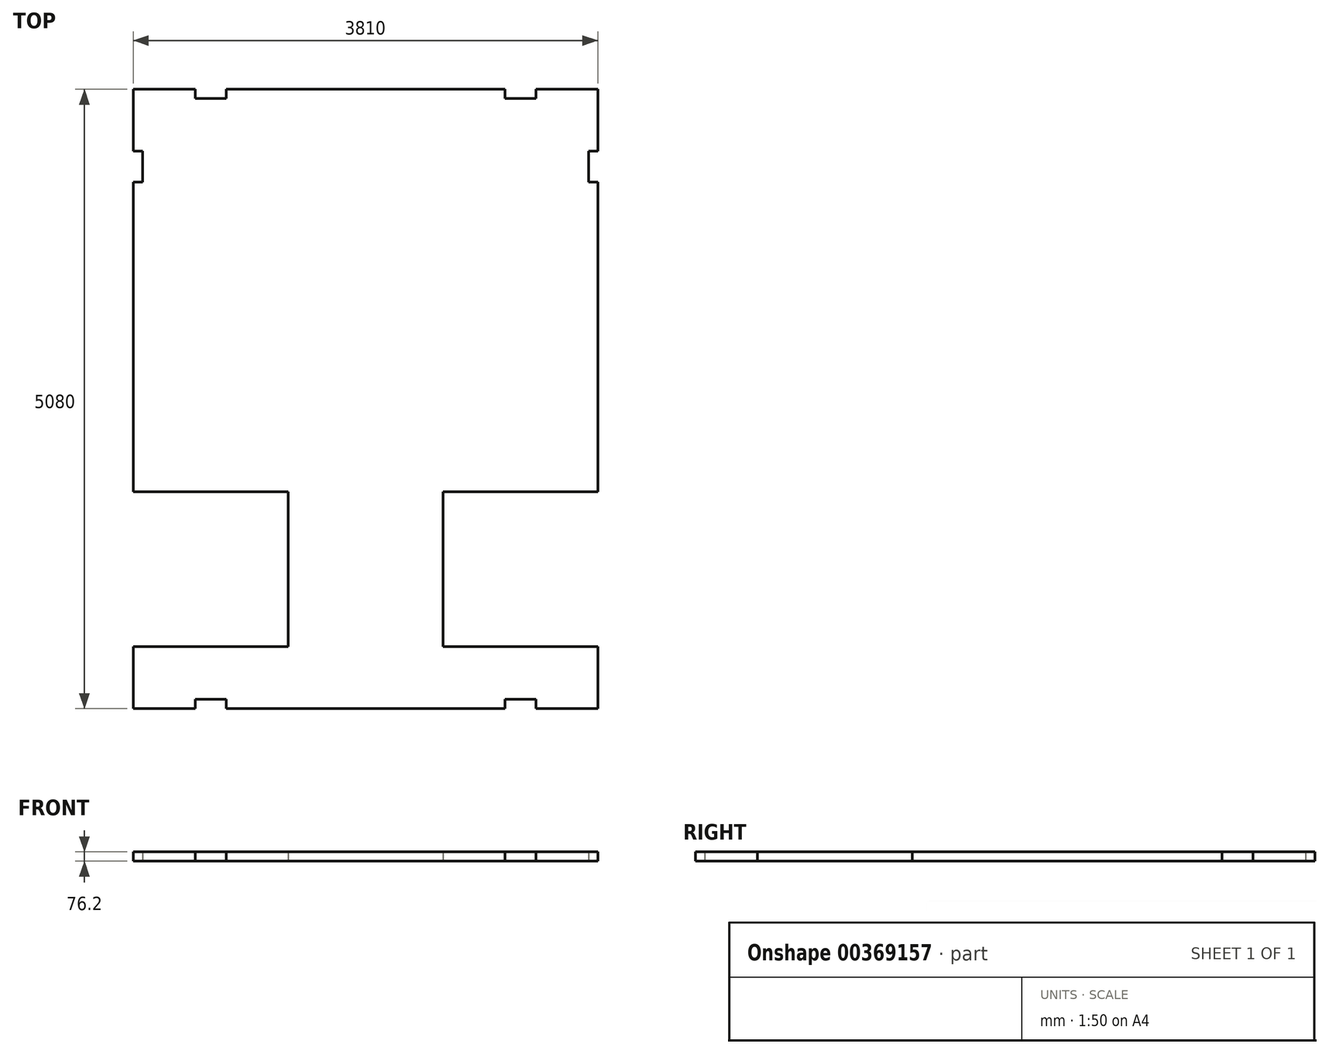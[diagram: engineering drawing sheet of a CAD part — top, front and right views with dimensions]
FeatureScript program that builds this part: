
annotation { "Feature Type Name" : "Feature", "Feature Type Description" : "" }
export const myFeature = defineFeature(function(context is Context, id is Id, definition is map)
    precondition{}
    {
        {
            var Q0;
            Q0=qCreatedBy(makeId("Top.planeOp"),FACE);
            var sketch = newSketch(context, id + "F0", { "sketchPlane" : qUnion([Q0])});
            skLineSegment(sketch, "E0.bottom", {"start": v(1905, 2540) * mm, "end": v(1397, 2540) * mm});
            skLineSegment(sketch, "E0.top", {"start": v(1143, -2540) * mm, "end": v(-1143, -2540) * mm});
            skLineSegment(sketch, "E0.left", {"start": v(1905, 2540) * mm, "end": v(1905, 2032) * mm});
            skLineSegment(sketch, "E0.right", {"start": v(-1905, 2540) * mm, "end": v(-1905, 2032) * mm});
            skPoint(sketch, "E0.middle", {"position": v(0, 0) * mm});
            skLineSegment(sketch, "E1", {"start": v(-1905, 1778) * mm, "end": v(-1828.8, 1778) * mm});
            skLineSegment(sketch, "E2", {"start": v(-1905, 2032) * mm, "end": v(-1828.8, 2032) * mm});
            skLineSegment(sketch, "E3", {"start": v(-1828.8, 2032) * mm, "end": v(-1828.8, 1778) * mm});
            skLineSegment(sketch, "E4.trimOffspring", {"start": v(-1905, 1778) * mm, "end": v(-1905, -762) * mm});
            skLineSegment(sketch, "E5", {"start": v(-1905, 2540) * mm, "end": v(-1397, 2540) * mm});
            skLineSegment(sketch, "E6", {"start": v(-1397, 2540) * mm, "end": v(-1143, 2540) * mm});
            skLineSegment(sketch, "E7", {"start": v(-1397, 2540) * mm, "end": v(-1397, 2463.8) * mm});
            skLineSegment(sketch, "E8", {"start": v(-1397, 2463.8) * mm, "end": v(-1143, 2463.8) * mm});
            skLineSegment(sketch, "E9", {"start": v(-1143, 2540) * mm, "end": v(-1143, 2463.8) * mm});
            skLineSegment(sketch, "E10", {"start": v(-1905, -2540) * mm, "end": v(-1905, -2032) * mm});
            skLineSegment(sketch, "E11", {"start": v(-1905, -2032) * mm, "end": v(-635, -2032) * mm});
            skLineSegment(sketch, "E12", {"start": v(-1905, -762) * mm, "end": v(-635, -762) * mm});
            skLineSegment(sketch, "E13", {"start": v(-635, -762) * mm, "end": v(-635, -2032) * mm});
            skLineSegment(sketch, "E14", {"start": v(-1905, -2540) * mm, "end": v(-1397, -2540) * mm});
            skLineSegment(sketch, "E15", {"start": v(-1397, -2540) * mm, "end": v(-1397, -2463.8) * mm});
            skLineSegment(sketch, "E16", {"start": v(-1397, -2463.8) * mm, "end": v(-1143, -2463.8) * mm});
            skLineSegment(sketch, "E17", {"start": v(-1143, -2463.8) * mm, "end": v(-1143, -2540) * mm});
            skLineSegment(sketch, "E18.trimOffspring", {"start": v(-1397, -2540) * mm, "end": v(-1905, -2540) * mm});
            skLineSegment(sketch, "E19", {"start": v(1905, -2540) * mm, "end": v(1397, -2540) * mm});
            skLineSegment(sketch, "E20", {"start": v(1397, -2540) * mm, "end": v(1397, -2463.8) * mm});
            skLineSegment(sketch, "E21", {"start": v(1397, -2463.8) * mm, "end": v(1143, -2463.8) * mm});
            skLineSegment(sketch, "E22", {"start": v(1143, -2463.8) * mm, "end": v(1143, -2540) * mm});
            skLineSegment(sketch, "E23", {"start": v(1905, -2540) * mm, "end": v(1905, -2032) * mm});
            skLineSegment(sketch, "E24", {"start": v(1905, -2032) * mm, "end": v(635, -2032) * mm});
            skLineSegment(sketch, "E25", {"start": v(635, -2032) * mm, "end": v(635, -762) * mm});
            skLineSegment(sketch, "E26", {"start": v(635, -762) * mm, "end": v(1905, -762) * mm});
            skLineSegment(sketch, "E27.trimOffspring", {"start": v(1905, -2032) * mm, "end": v(1905, -2540) * mm});
            skLineSegment(sketch, "E28", {"start": v(1905, 2032) * mm, "end": v(1828.8, 2032) * mm});
            skLineSegment(sketch, "E29", {"start": v(1828.8, 2032) * mm, "end": v(1828.8, 1778) * mm});
            skLineSegment(sketch, "E30", {"start": v(1905, 1778) * mm, "end": v(1828.8, 1778) * mm});
            skLineSegment(sketch, "E31.trimOffspring", {"start": v(1905, 1778) * mm, "end": v(1905, -762) * mm});
            skLineSegment(sketch, "E32", {"start": v(1397, 2540) * mm, "end": v(1397, 2463.8) * mm});
            skLineSegment(sketch, "E33", {"start": v(1143, 2540) * mm, "end": v(1143, 2463.8) * mm});
            skLineSegment(sketch, "E34", {"start": v(1397, 2463.8) * mm, "end": v(1143, 2463.8) * mm});
            skLineSegment(sketch, "E35.trimOffspring", {"start": v(1143, 2540) * mm, "end": v(-1905, 2540) * mm});
            skLineSegment(sketch, "E36.trimOffspring", {"start": v(-1905, -2032) * mm, "end": v(-1905, -2540) * mm});
            skSolve(sketch);
        }
        {
            var Q0;
            Q0=makeQuery(id+"F0.imprint","IMPRINT",FACE,{"disambiguationData":[TD([[makeQuery(id+"F0.imprint","IMPRINT",EDGE,{"derivedFrom":sQuery(id+"F0.wireOp",EDGE,"E0.top")}),-1.0]])]});
            extrude(context, id + "F1", {"entities" : qUnion([Q0]), "depth" : 76.2 * mm});
        }
    });
